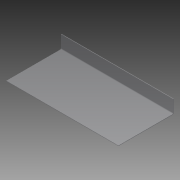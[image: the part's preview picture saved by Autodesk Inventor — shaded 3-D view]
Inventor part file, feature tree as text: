
AUTODESK INVENTOR PART (.ipt)
format: ipt  version: 2014 SP1 (Build 180222100, 222)  size: 86,016 bytes
history: native  units: in
note: dims shown in document units (in); Inventor stores cm internally (conversion verified against a paired STEP export)
features: sketch x2, extrude x1, other x1
ambient origin geometry x8: Origin, YZ Plane, XZ Plane, XY Plane, X Axis, Y Axis, Z Axis, Center Point
bodies: Solid1 (feature_tree)
feature tree (4):
  extrude  "Extrusion1"  Depth=12.5in
  other  "Bend Part1"
  sketch  "Sketch1"  dims[d0=12.5in d1=7.5in]
  sketch  "Sketch2"  dims[d2=0.0625in d3=0.0in d4=1.5in d5=0.1in d6=90.0deg]
